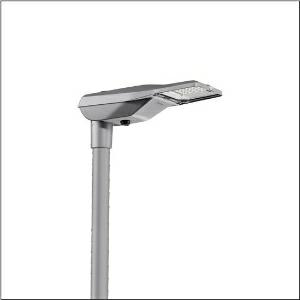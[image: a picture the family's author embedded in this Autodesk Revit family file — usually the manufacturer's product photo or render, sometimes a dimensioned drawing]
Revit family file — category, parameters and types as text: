
# Revit family: streetlight_sl_21_micro___st1_0a_5xe1d33r08db_e2a0
name_source: partatom
category: Lighting Fixtures
units: mm (PartAtom-declared; Revit-internal decimal feet)

## family parameters
Cut with Voids When Loaded = No
Host = Face
Light Source = No
Part Type = Normal
Room Calculation Point = No
Round Connector Dimension = Use Diameter
Shared = No

## types (1)
- --- (1 x LED, 5110 lm, 39.1 W, 3000K)
    Apparent Load = 39 VA
    CIE Flux Codes = 37 72 97 100 100
    Color Rendering = 70
    Color Temperature = 3000K
    Default Elevation = 1800 mm
    Description = Streetlight SL 21 micro, mast luminaire, primary light control with lens, of PMMA, primary optical cover: cover, of toughened safety glass, transparent, light distribution: ST1.0a, light emission: direct distribution, primary light characteristic: asymmetric, installation type: side-entry, post-top, LED, High Power LED, rated luminous flux: 5.110lm, luminous efficacy: 131lm/W, light colour: 730, colour temperature: 3000K, control gear: D4i, control: flexible luminous flux parameterisation, time-dependent luminous flux control, constant luminous flux control, overheat protection, pre-setting: logarithmic dimming characteristic, mains connection: 220..240V, AC, 50/60Hz, start of lifetime: 39W, end of service life: 41W, reduction: 18W, luminaire housing, of diecast aluminium, powder-coated, SITECO metallic grey (DB 702S), corrosivity category C5 high according to DIN EN ISO 12944, please order mast flange separately, inclination adjustable: 0°, 5°, 10°, 15°, sealing non-destructively replaceable, multi-level sealing system, length: 528mm, width: 235mm, height: 110mm, mast flange for spigot size: 42mm (side-entry): 5XC10008XM4, 60/48mm (side-entry/post-top): 5XC10108XM2, 76/60mm (side-entry/post-top): 5XC10108XM1, Smart Interface below, protection rating (complete): IP66, insulation class (complete): insulation class II (safety insulation), certification: CE, ENEC, ENEC+, VDE, impact resistance: IK10, permissible operating ambient temperature for outdoor applications: -40..+50°C, standard-compliant lighting for roads and squares, packaging unit: 1 piece

Light Distribution: ST1.0a
    Height = 110 mm
    Lamp = 1 x LED
    Lamp Light Flux = 5110 lm
    Lamp Power = 39.1 W
    Lamp count = 1
    Length = 528 mm
    Luminous efficacy = 131 lm/W
    Manufacturer = Siteco
    ModVariant = No
    Model = 5XE1D33R08DB
    Number of Poles = 1
    OnlyDefault = Yes
    Power Factor = 1
    Product Name = Streetlight SL 21 micro | ST1.0a
    Product group = mast luminaire | pylon top
    ProductGroupID = 6100
    Protection Class = Protection class II
    Protection Degree = IP 66
    RLX_Detail_Level = 1
    RLX_Emergency_Light_Flux = 0 lm
    RLX_Emergency_Type = 0
    RLX_Emergency_Type_DB = No
    RlxData = <blob elided: 98557 chars, md5=eba4b2bb>
    Socket = socket
    Standby Power = 0 W
    System Light Flux = 5110 lm
    System Power = 39 W
    Type Comments = factory setting: luminous flux: 100 % | dim-lin: 254 | 765 mA
    Type Image = l_1277290.jpg
    URL = http://relux.com
    VarID = @adj_155365
    Voltage = 0 V
    Weight = 0.00 kg
    Width = 235 mm

## geometry (parser evidence)
native form markers: Blend x4, Sweep x10
no freeform markers — native parametric forms only
